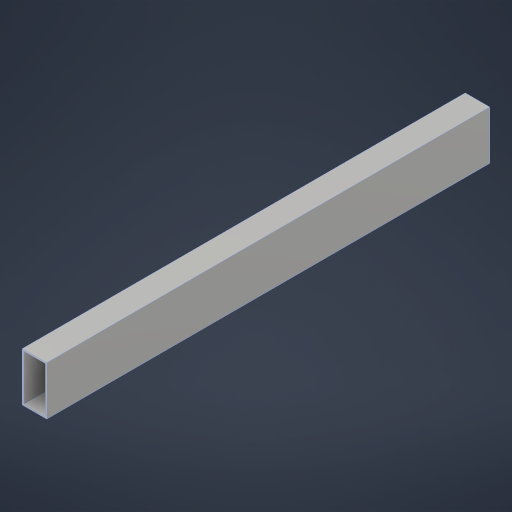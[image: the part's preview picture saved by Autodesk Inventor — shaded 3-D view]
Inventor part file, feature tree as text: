
AUTODESK INVENTOR PART (.ipt)
format: ipt  version: 2024.2 (Build 282272000, 272)  size: 172,032 bytes
history: native  units: in
note: dims shown in document units (in); Inventor stores cm internally (conversion verified against a paired STEP export)
features: extrude x1
ambient origin geometry x8: Origin, YZ Plane, XZ Plane, XY Plane, X Axis, Y Axis, Z Axis, Center Point
bodies: Solid1 (feature_tree)
feature tree (1):
  extrude  "Extrusion1"  TaperAngle=0.0deg  [1 undecoded]
note: 1 required parameter value undecoded (feature->parameter linkage not recoverable at this tier; creation-order binding heuristic only, values carry confidence <= 0.55)
